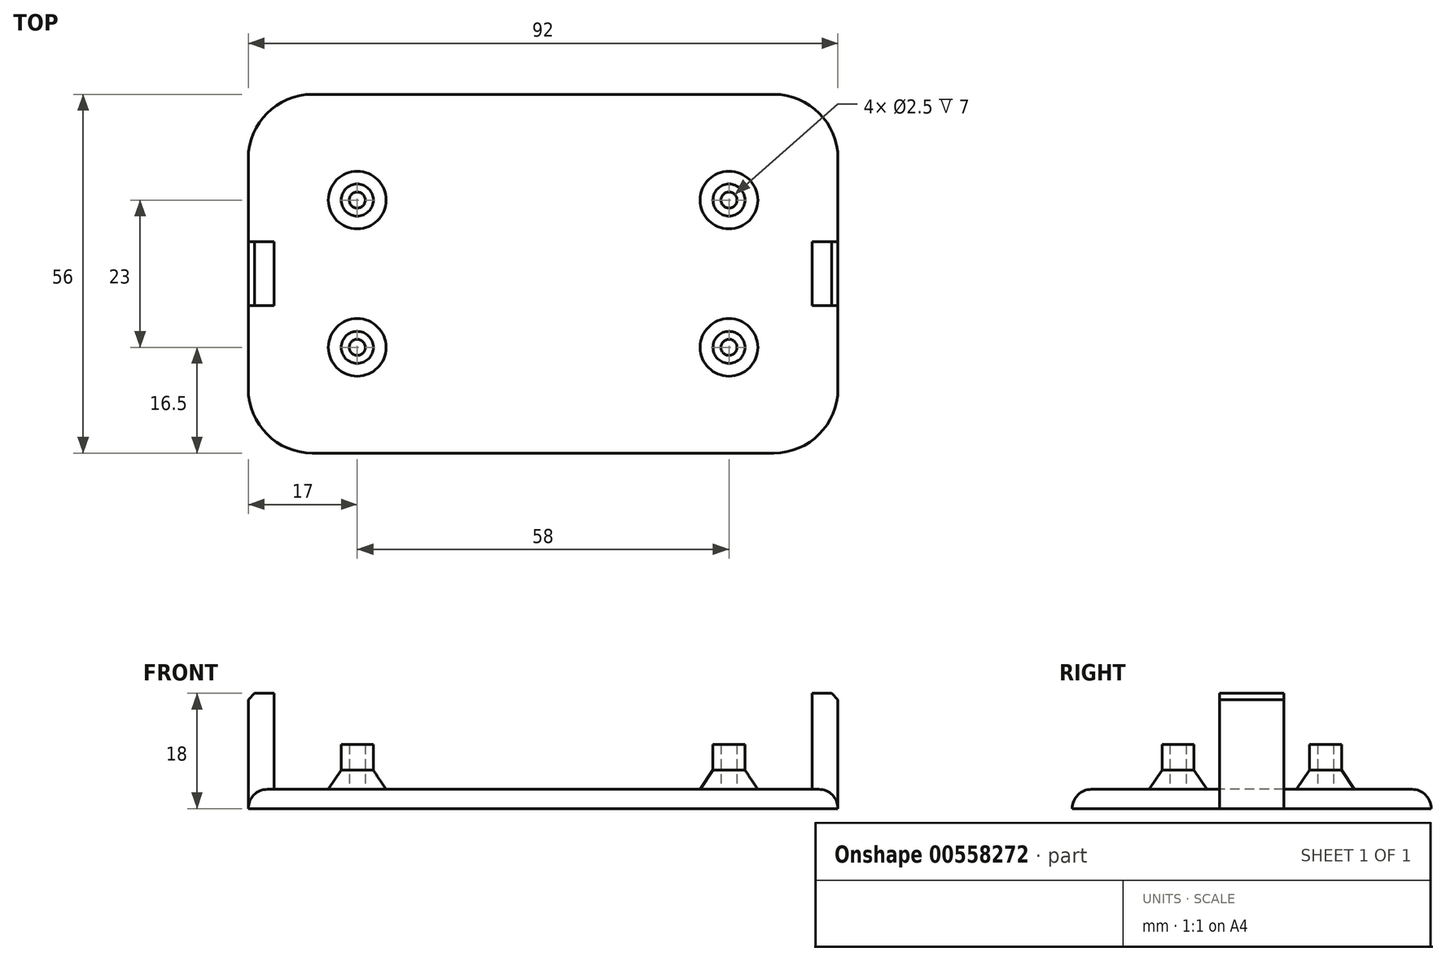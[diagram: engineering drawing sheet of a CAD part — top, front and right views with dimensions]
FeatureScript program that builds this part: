
annotation { "Feature Type Name" : "Feature", "Feature Type Description" : "" }
export const myFeature = defineFeature(function(context is Context, id is Id, definition is map)
    precondition{}
    {
        {
            var Q0;
            Q0=qCreatedBy(makeId("Top.planeOp"),FACE);
            var sketch = newSketch(context, id + "F0", { "sketchPlane" : qUnion([Q0])});
            skLineSegment(sketch, "E0.bottom", {"start": v(36, 28) * mm, "end": v(-36, 28) * mm});
            skLineSegment(sketch, "E0.top", {"start": v(36, -28) * mm, "end": v(-36, -28) * mm});
            skLineSegment(sketch, "E0.left", {"start": v(46, 18) * mm, "end": v(46, -18) * mm});
            skLineSegment(sketch, "E0.right", {"start": v(-46, 18) * mm, "end": v(-46, -18) * mm});
            skPoint(sketch, "E0.middle", {"position": v(0, 0) * mm});
            skPoint(sketch, "E1.visualSharp", {"position": v(-46, 28) * mm});
            skArc(sketch, "E1.filletArc", {"start": v(-36, 28) * mm, "mid": v(-43.07, 25.07) * mm, "end": v(-46, 18) * mm});
            skPoint(sketch, "E2.visualSharp", {"position": v(-46, -28) * mm});
            skArc(sketch, "E2.filletArc", {"start": v(-46, -18) * mm, "mid": v(-43.07, -25.07) * mm, "end": v(-36, -28) * mm});
            skPoint(sketch, "E3.visualSharp", {"position": v(46, -28) * mm});
            skArc(sketch, "E3.filletArc", {"start": v(36, -28) * mm, "mid": v(43.07, -25.07) * mm, "end": v(46, -18) * mm});
            skPoint(sketch, "E4.visualSharp", {"position": v(46, 28) * mm});
            skArc(sketch, "E4.filletArc", {"start": v(46, 18) * mm, "mid": v(43.07, 25.07) * mm, "end": v(36, 28) * mm});
            skSolve(sketch);
        }
        {
            var Q0;
            Q0=qCreatedBy(makeId("Top.planeOp"),FACE);
            var sketch = newSketch(context, id + "F1", { "sketchPlane" : qUnion([Q0])});
            skPoint(sketch, "E5", {"position": v(-32.5, 15) * mm});
            skPoint(sketch, "E6", {"position": v(32.5, 15) * mm});
            skPoint(sketch, "E7", {"position": v(32.5, -15) * mm});
            skPoint(sketch, "E8", {"position": v(-32.5, -15) * mm});
            skLineSegment(sketch, "E9", {"start": v(-29.5, 15) * mm, "end": v(29.5, 15) * mm, "construction": true});
            skLineSegment(sketch, "E10", {"start": v(32.5, 12) * mm, "end": v(32.5, -12) * mm, "construction": true});
            skLineSegment(sketch, "E11.MirrorCS", {"start": v(-29.5, -15) * mm, "end": v(29.5, -15) * mm, "construction": true});
            skLineSegment(sketch, "E12.MirrorCS", {"start": v(-32.5, 12) * mm, "end": v(-32.5, -12) * mm, "construction": true});
            skArc(sketch, "E13.filletArc", {"start": v(32.5, 12) * mm, "mid": v(31.62, 14.12) * mm, "end": v(29.5, 15) * mm, "construction": true});
            skArc(sketch, "E14.filletArc", {"start": v(-29.5, 15) * mm, "mid": v(-31.62, 14.12) * mm, "end": v(-32.5, 12) * mm, "construction": true});
            skArc(sketch, "E15.filletArc", {"start": v(-32.5, -12) * mm, "mid": v(-31.62, -14.12) * mm, "end": v(-29.5, -15) * mm, "construction": true});
            skArc(sketch, "E16.filletArc", {"start": v(29.5, -15) * mm, "mid": v(31.62, -14.12) * mm, "end": v(32.5, -12) * mm, "construction": true});
            skCircle(sketch, "E17", {"center": v(-29, 11.5) * mm, "radius": 1.25 * mm});
            skCircle(sketch, "E18.MirrorC", {"center": v(29, 11.5) * mm, "radius": 1.25 * mm});
            skCircle(sketch, "E19.MirrorC", {"center": v(-29, -11.5) * mm, "radius": 1.25 * mm});
            skCircle(sketch, "E20.MirrorC", {"center": v(29, -11.5) * mm, "radius": 1.25 * mm});
            skCircle(sketch, "E21", {"center": v(-29, 11.5) * mm, "radius": 2.5 * mm});
            skCircle(sketch, "E22.MirrorC", {"center": v(29, 11.5) * mm, "radius": 2.5 * mm});
            skCircle(sketch, "E23.MirrorC", {"center": v(-29, -11.5) * mm, "radius": 2.5 * mm});
            skCircle(sketch, "E24.MirrorC", {"center": v(29, -11.5) * mm, "radius": 2.5 * mm});
            skSolve(sketch);
        }
        {
            var Q0;
            Q0=makeQuery(id+"F0.imprint","IMPRINT",FACE,{"disambiguationData":[TD([[makeQuery(id+"F0.imprint","IMPRINT",EDGE,{"derivedFrom":sQuery(id+"F0.wireOp",EDGE,"E0.bottom")}),1.0]])]});
            extrude(context, id + "F2", {"entities" : qUnion([Q0]), "depth" : 3 * mm, "offsetDistance" : 25 * mm});
        }
        {
            var Q0;
            Q0 = qSketchRegion(id + "F1", true);
            extrude(context, id + "F3", {"entities" : qUnion([Q0]), "operationType" : NewBodyOperationType.ADD, "depth" : 10 * mm, "offsetDistance" : 25 * mm});
        }
        {
            var Q0;
            Q0=makeQuery(id+"F3.boolean.opBoolean","INTERSECT",EDGE,{"derivedFrom":[makeQuery(id+"F2.opExtrude","CAP_FACE",FACE,{"disambiguationData":[OSD([sQuery(id+"F0.wireOp",EDGE,"E0.bottom"),sQuery(id+"F0.wireOp",EDGE,"E0.top"),sQuery(id+"F0.wireOp",EDGE,"E0.left"),sQuery(id+"F0.wireOp",EDGE,"E0.right"),sQuery(id+"F0.wireOp",EDGE,"E1.filletArc"),sQuery(id+"F0.wireOp",EDGE,"E2.filletArc"),sQuery(id+"F0.wireOp",EDGE,"E3.filletArc"),sQuery(id+"F0.wireOp",EDGE,"E4.filletArc")])],"isStart":false}),makeQuery(id+"F3.opExtrude","SWEPT_FACE",FACE,{"disambiguationData":[OSD([sQuery(id+"F1.wireOp",EDGE,"E21")])]})]});
            var Q1;
            Q1=makeQuery(id+"F3.boolean.opBoolean","INTERSECT",EDGE,{"derivedFrom":[makeQuery(id+"F2.opExtrude","CAP_FACE",FACE,{"disambiguationData":[OSD([sQuery(id+"F0.wireOp",EDGE,"E0.bottom"),sQuery(id+"F0.wireOp",EDGE,"E0.top"),sQuery(id+"F0.wireOp",EDGE,"E0.left"),sQuery(id+"F0.wireOp",EDGE,"E0.right"),sQuery(id+"F0.wireOp",EDGE,"E1.filletArc"),sQuery(id+"F0.wireOp",EDGE,"E2.filletArc"),sQuery(id+"F0.wireOp",EDGE,"E3.filletArc"),sQuery(id+"F0.wireOp",EDGE,"E4.filletArc")])],"isStart":false}),makeQuery(id+"F3.opExtrude","SWEPT_FACE",FACE,{"disambiguationData":[OSD([sQuery(id+"F1.wireOp",EDGE,"E22.MirrorC")])]})]});
            var Q2;
            Q2=makeQuery(id+"F3.boolean.opBoolean","INTERSECT",EDGE,{"derivedFrom":[makeQuery(id+"F2.opExtrude","CAP_FACE",FACE,{"disambiguationData":[OSD([sQuery(id+"F0.wireOp",EDGE,"E0.bottom"),sQuery(id+"F0.wireOp",EDGE,"E0.top"),sQuery(id+"F0.wireOp",EDGE,"E0.left"),sQuery(id+"F0.wireOp",EDGE,"E0.right"),sQuery(id+"F0.wireOp",EDGE,"E1.filletArc"),sQuery(id+"F0.wireOp",EDGE,"E2.filletArc"),sQuery(id+"F0.wireOp",EDGE,"E3.filletArc"),sQuery(id+"F0.wireOp",EDGE,"E4.filletArc")])],"isStart":false}),makeQuery(id+"F3.opExtrude","SWEPT_FACE",FACE,{"disambiguationData":[OSD([sQuery(id+"F1.wireOp",EDGE,"E24.MirrorC")])]})]});
            var Q3;
            Q3=makeQuery(id+"F3.boolean.opBoolean","INTERSECT",EDGE,{"derivedFrom":[makeQuery(id+"F2.opExtrude","CAP_FACE",FACE,{"disambiguationData":[OSD([sQuery(id+"F0.wireOp",EDGE,"E0.bottom"),sQuery(id+"F0.wireOp",EDGE,"E0.top"),sQuery(id+"F0.wireOp",EDGE,"E0.left"),sQuery(id+"F0.wireOp",EDGE,"E0.right"),sQuery(id+"F0.wireOp",EDGE,"E1.filletArc"),sQuery(id+"F0.wireOp",EDGE,"E2.filletArc"),sQuery(id+"F0.wireOp",EDGE,"E3.filletArc"),sQuery(id+"F0.wireOp",EDGE,"E4.filletArc")])],"isStart":false}),makeQuery(id+"F3.opExtrude","SWEPT_FACE",FACE,{"disambiguationData":[OSD([sQuery(id+"F1.wireOp",EDGE,"E23.MirrorC")])]})]});
            chamfer(context, id + "F4", {"entities" : qUnion([Q0, Q1, Q2, Q3]), "chamferType" : ChamferType.TWO_OFFSETS, "width1" : 2 * mm, "oppositeDirection" : false, "width2" : 3 * mm, "tangentPropagation" : true});
        }
        {
            var Q0;
            Q0=makeQuery(id+"F2.opExtrude","CAP_EDGE",EDGE,{"disambiguationData":[OSD([sQuery(id+"F0.wireOp",EDGE,"E0.bottom")])],"isStart":false});
            fillet(context, id + "F5", {"entities" : qUnion([Q0]), "radius" : 3 * mm, "tangentPropagation" : true, "allowEdgeOverflow" : false});
        }
        {
            var Q0;
            Q0=qCreatedBy(makeId("Right.planeOp"),FACE);
            cPlane(context, id + "F6", {"entities" : qUnion([Q0]), "cplaneType" : CPlaneType.OFFSET, "offset" : 46 * mm, "width" : 150 * mm, "height" : 150 * mm});
        }
        {
            var Q0;
            Q0=qCreatedBy(id+"F6.planeOp",FACE);
            var sketch = newSketch(context, id + "F7", { "sketchPlane" : qUnion([Q0])});
            skLineSegment(sketch, "E25", {"start": v(-5, 0) * mm, "end": v(-5, 18) * mm});
            skLineSegment(sketch, "E26", {"start": v(-5, 18) * mm, "end": v(5, 18) * mm});
            skLineSegment(sketch, "E27", {"start": v(5, 18) * mm, "end": v(5, 0) * mm});
            skLineSegment(sketch, "E28", {"start": v(-5, 0) * mm, "end": v(5, 0) * mm});
            skSolve(sketch);
        }
        {
            var Q0;
            Q0=makeQuery(id+"F7.imprint","IMPRINT",FACE,{"disambiguationData":[TD([[makeQuery(id+"F7.imprint","IMPRINT",EDGE,{"derivedFrom":sQuery(id+"F7.wireOp",EDGE,"E25")}),-1.0]])]});
            extrude(context, id + "F8", {"entities" : qUnion([Q0]), "oppositeDirection" : true, "depth" : 4 * mm, "offsetDistance" : 25 * mm});
        }
        {
            var Q0;
            Q0=makeQuery(id+"F8.opExtrude","SWEPT_BODY",BODY,{"disambiguationData":[OSD([sQuery(id+"F7.wireOp",EDGE,"E25"),sQuery(id+"F7.wireOp",EDGE,"E26"),sQuery(id+"F7.wireOp",EDGE,"E27"),sQuery(id+"F7.wireOp",EDGE,"E28")])]});
            var Q1;
            Q1=qCreatedBy(makeId("Right.planeOp"),FACE);
            mirror(context, id + "F9", {"operationType" : NewBodyOperationType.ADD, "entities" : qUnion([Q0]), "mirrorPlane" : qUnion([Q1])});
        }
        {
            var Q0;
            Q0=makeQuery(id+"F9.opPattern","COPY",EDGE,{"derivedFrom":makeQuery(id+"F8.opExtrude","CAP_EDGE",EDGE,{"disambiguationData":[OSD([sQuery(id+"F7.wireOp",EDGE,"E26")])],"isStart":true}),"instanceName":"1"});
            var Q1;
            Q1=makeQuery(id+"F8.opExtrude","CAP_EDGE",EDGE,{"disambiguationData":[OSD([sQuery(id+"F7.wireOp",EDGE,"E26")])],"isStart":true});
            chamfer(context, id + "F10", {"entities" : qUnion([Q0, Q1]), "width" : 1 * mm, "tangentPropagation" : true});
        }
    });
